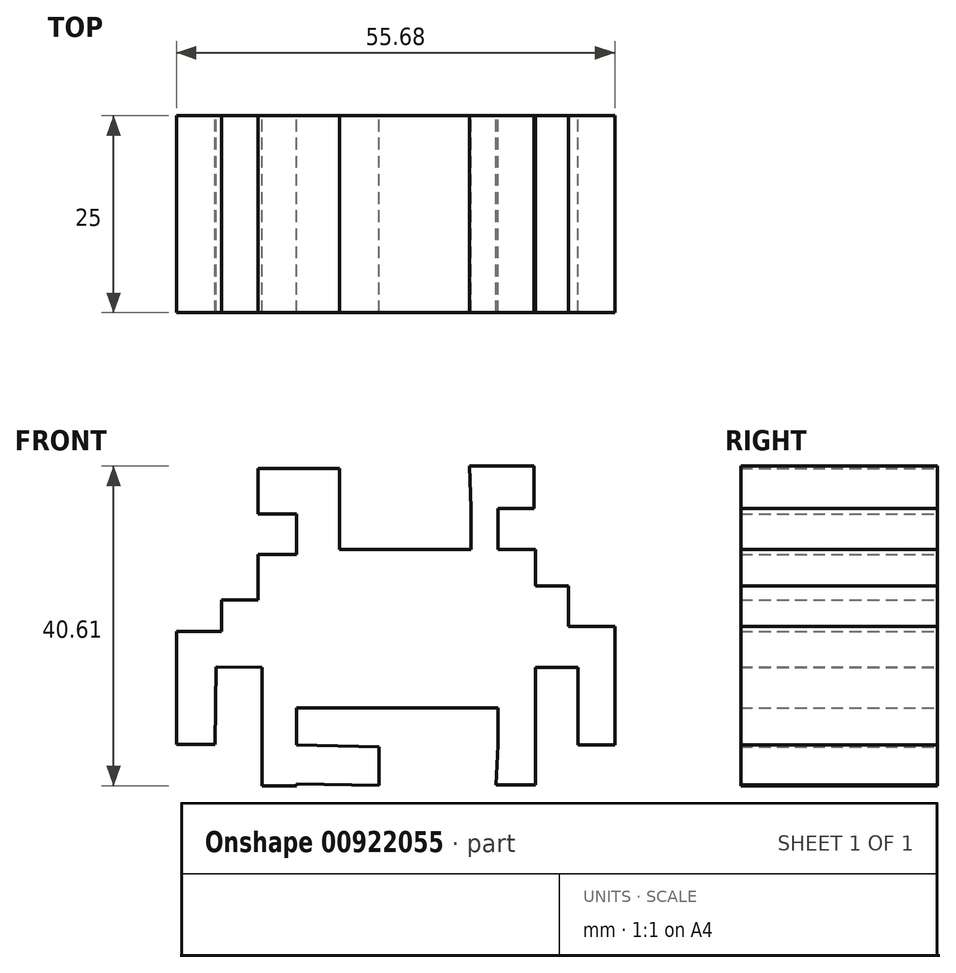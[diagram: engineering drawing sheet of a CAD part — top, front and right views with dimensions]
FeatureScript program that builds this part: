
annotation { "Feature Type Name" : "Feature", "Feature Type Description" : "" }
export const myFeature = defineFeature(function(context is Context, id is Id, definition is map)
    precondition{}
    {
        {
            var Q0;
            Q0=qCreatedBy(makeId("Front.planeOp"),FACE);
            var sketch = newSketch(context, id + "F0", { "sketchPlane" : qUnion([Q0])});
            skLineSegment(sketch, "E0", {"start": v(10.78, 21.99) * mm, "end": v(10.78, 36.36) * mm});
            skLineSegment(sketch, "E1", {"start": v(11.93, 36.36) * mm, "end": v(16.53, 36.36) * mm});
            skLineSegment(sketch, "E2", {"start": v(16.53, 36.36) * mm, "end": v(16.53, 40.38) * mm});
            skLineSegment(sketch, "E3", {"start": v(16.53, 40.38) * mm, "end": v(21.12, 40.38) * mm});
            skLineSegment(sketch, "E4", {"start": v(21.12, 40.38) * mm, "end": v(21.12, 46.13) * mm});
            skLineSegment(sketch, "E5", {"start": v(21.12, 46.13) * mm, "end": v(26.01, 46.13) * mm});
            skLineSegment(sketch, "E6", {"start": v(26.01, 46.13) * mm, "end": v(26.01, 51.3) * mm});
            skLineSegment(sketch, "E7", {"start": v(26.01, 51.3) * mm, "end": v(21.12, 51.3) * mm});
            skLineSegment(sketch, "E8", {"start": v(21.12, 51.3) * mm, "end": v(21.12, 57.05) * mm});
            skLineSegment(sketch, "E9", {"start": v(21.12, 57.05) * mm, "end": v(26.01, 57.05) * mm});
            skLineSegment(sketch, "E10", {"start": v(26.01, 57.05) * mm, "end": v(26.01, 51.3) * mm});
            skLineSegment(sketch, "E11", {"start": v(26.01, 57.05) * mm, "end": v(31.47, 57.05) * mm});
            skLineSegment(sketch, "E12", {"start": v(31.47, 51.3) * mm, "end": v(31.47, 57.05) * mm});
            skLineSegment(sketch, "E13", {"start": v(31.47, 51.3) * mm, "end": v(26.01, 51.3) * mm});
            skLineSegment(sketch, "E14", {"start": v(31.47, 51.3) * mm, "end": v(31.47, 46.75) * mm});
            skLineSegment(sketch, "E15", {"start": v(31.77, 46.75) * mm, "end": v(48.16, 46.75) * mm});
            skLineSegment(sketch, "E16", {"start": v(48.16, 46.75) * mm, "end": v(48.16, 52) * mm});
            skLineSegment(sketch, "E17", {"start": v(48.16, 52) * mm, "end": v(51.59, 52) * mm});
            skLineSegment(sketch, "E18", {"start": v(51.59, 51.78) * mm, "end": v(51.59, 57.37) * mm});
            skLineSegment(sketch, "E19", {"start": v(51.59, 57.37) * mm, "end": v(56.17, 57.37) * mm});
            skLineSegment(sketch, "E20", {"start": v(56.17, 57.37) * mm, "end": v(56.17, 52) * mm});
            skLineSegment(sketch, "E21", {"start": v(56.17, 52) * mm, "end": v(51.59, 52) * mm});
            skLineSegment(sketch, "E22", {"start": v(51.59, 46.75) * mm, "end": v(51.59, 52) * mm});
            skLineSegment(sketch, "E23", {"start": v(51.59, 46.75) * mm, "end": v(56.4, 46.75) * mm});
            skLineSegment(sketch, "E24", {"start": v(56.4, 46.97) * mm, "end": v(56.4, 42.17) * mm});
            skLineSegment(sketch, "E25", {"start": v(56.4, 42.17) * mm, "end": v(60.53, 42.17) * mm});
            skLineSegment(sketch, "E26", {"start": v(60.53, 42.17) * mm, "end": v(60.53, 37.02) * mm});
            skLineSegment(sketch, "E27", {"start": v(60.53, 37.02) * mm, "end": v(61.1, 37.02) * mm});
            skLineSegment(sketch, "E28", {"start": v(61.1, 37.02) * mm, "end": v(66.46, 37.02) * mm});
            skLineSegment(sketch, "E29", {"start": v(66.46, 37.02) * mm, "end": v(66.46, 21.92) * mm});
            skLineSegment(sketch, "E30", {"start": v(66.57, 21.92) * mm, "end": v(61.76, 21.92) * mm});
            skLineSegment(sketch, "E31", {"start": v(61.76, 21.92) * mm, "end": v(61.76, 31.77) * mm});
            skLineSegment(sketch, "E32", {"start": v(61.76, 31.77) * mm, "end": v(56.4, 31.77) * mm});
            skLineSegment(sketch, "E33", {"start": v(56.4, 31.77) * mm, "end": v(56.4, 21.92) * mm});
            skLineSegment(sketch, "E34", {"start": v(56.4, 21.92) * mm, "end": v(51.59, 21.92) * mm});
            skLineSegment(sketch, "E35", {"start": v(56.4, 17.34) * mm, "end": v(56.4, 21.92) * mm});
            skLineSegment(sketch, "E36", {"start": v(51.59, 21.92) * mm, "end": v(51.59, 26.62) * mm});
            skLineSegment(sketch, "E37", {"start": v(51.81, 26.62) * mm, "end": v(26.01, 26.62) * mm});
            skLineSegment(sketch, "E38", {"start": v(26.01, 26.62) * mm, "end": v(26.01, 21.92) * mm});
            skLineSegment(sketch, "E39", {"start": v(26.01, 21.92) * mm, "end": v(26.01, 16.76) * mm});
            skLineSegment(sketch, "E40", {"start": v(26.01, 16.76) * mm, "end": v(21.62, 16.76) * mm});
            skLineSegment(sketch, "E41", {"start": v(21.62, 16.76) * mm, "end": v(21.62, 21.92) * mm});
            skLineSegment(sketch, "E42", {"start": v(21.62, 21.92) * mm, "end": v(21.62, 21.37) * mm});
            skLineSegment(sketch, "E43", {"start": v(10.78, 21.99) * mm, "end": v(15.7, 21.99) * mm});
            skLineSegment(sketch, "E44", {"start": v(15.8, 31.88) * mm, "end": v(21.62, 31.77) * mm});
            skLineSegment(sketch, "E45", {"start": v(21.62, 31.77) * mm, "end": v(21.62, 21.92) * mm});
            skLineSegment(sketch, "E46", {"start": v(26.01, 21.92) * mm, "end": v(21.62, 21.92) * mm});
            skLineSegment(sketch, "E47", {"start": v(26.01, 21.92) * mm, "end": v(36.5, 21.72) * mm});
            skLineSegment(sketch, "E48", {"start": v(36.5, 16.78) * mm, "end": v(36.5, 21.72) * mm});
            skLineSegment(sketch, "E49", {"start": v(36.5, 16.78) * mm, "end": v(26.01, 16.98) * mm});
            skLineSegment(sketch, "E50", {"start": v(15.76, 31.9) * mm, "end": v(17.37, 31.85) * mm});
            skLineSegment(sketch, "E51", {"start": v(15.8, 31.88) * mm, "end": v(15.7, 21.99) * mm});
            skLineSegment(sketch, "E52", {"start": v(31.77, 46.75) * mm, "end": v(31.47, 46.75) * mm});
            skLineSegment(sketch, "E53", {"start": v(11.93, 36.36) * mm, "end": v(10.78, 36.36) * mm});
            skLineSegment(sketch, "E54", {"start": v(51.59, 57.37) * mm, "end": v(48, 57.37) * mm});
            skLineSegment(sketch, "E55", {"start": v(48, 57.37) * mm, "end": v(48.16, 52) * mm});
            skLineSegment(sketch, "E56", {"start": v(51.38, 16.87) * mm, "end": v(56.2, 16.87) * mm});
            skLineSegment(sketch, "E57", {"start": v(51.38, 16.87) * mm, "end": v(51.59, 21.92) * mm});
            skLineSegment(sketch, "E58", {"start": v(56.4, 17.34) * mm, "end": v(56.4, 16.87) * mm});
            skLineSegment(sketch, "E59", {"start": v(56.4, 16.87) * mm, "end": v(56.2, 16.87) * mm});
            skSolve(sketch);
        }
        {
            var Q0;
            Q0=qCreatedBy(makeId("Front.planeOp"),FACE);
            var sketch = newSketch(context, id + "F1", { "sketchPlane" : qUnion([Q0])});
            skLineSegment(sketch, "E60", {"start": v(11.89, 36.3) * mm, "end": v(10.63, 36.3) * mm});
            skSolve(sketch);
        }
        {
            var Q0;
            Q0 = qSketchRegion(id + "F1", true);
            var Q1;
            Q1 = qSketchRegion(id + "F0", true);
            extrude(context, id + "F2", {"entities" : qUnion([Q0, Q1]), "depth" : 25 * mm, "offsetDistance" : 25 * mm});
        }
        {
            var Q0;
            Q0 = qSketchRegion(id + "F0", true);
            extrude(context, id + "F3", {"entities" : qUnion([Q0]), "depth" : 25 * mm, "offsetDistance" : 25 * mm});
        }
        {
            var Q0;
            Q0 = qSketchRegion(id + "F0", true);
            extrude(context, id + "F4", {"entities" : qUnion([Q0]), "depth" : 25 * mm, "offsetDistance" : 25 * mm});
        }
        {
            var Q0;
            Q0 = qSketchRegion(id + "F0", true);
            extrude(context, id + "F5", {"entities" : qUnion([Q0]), "depth" : 25 * mm, "offsetDistance" : 25 * mm});
        }
    });
